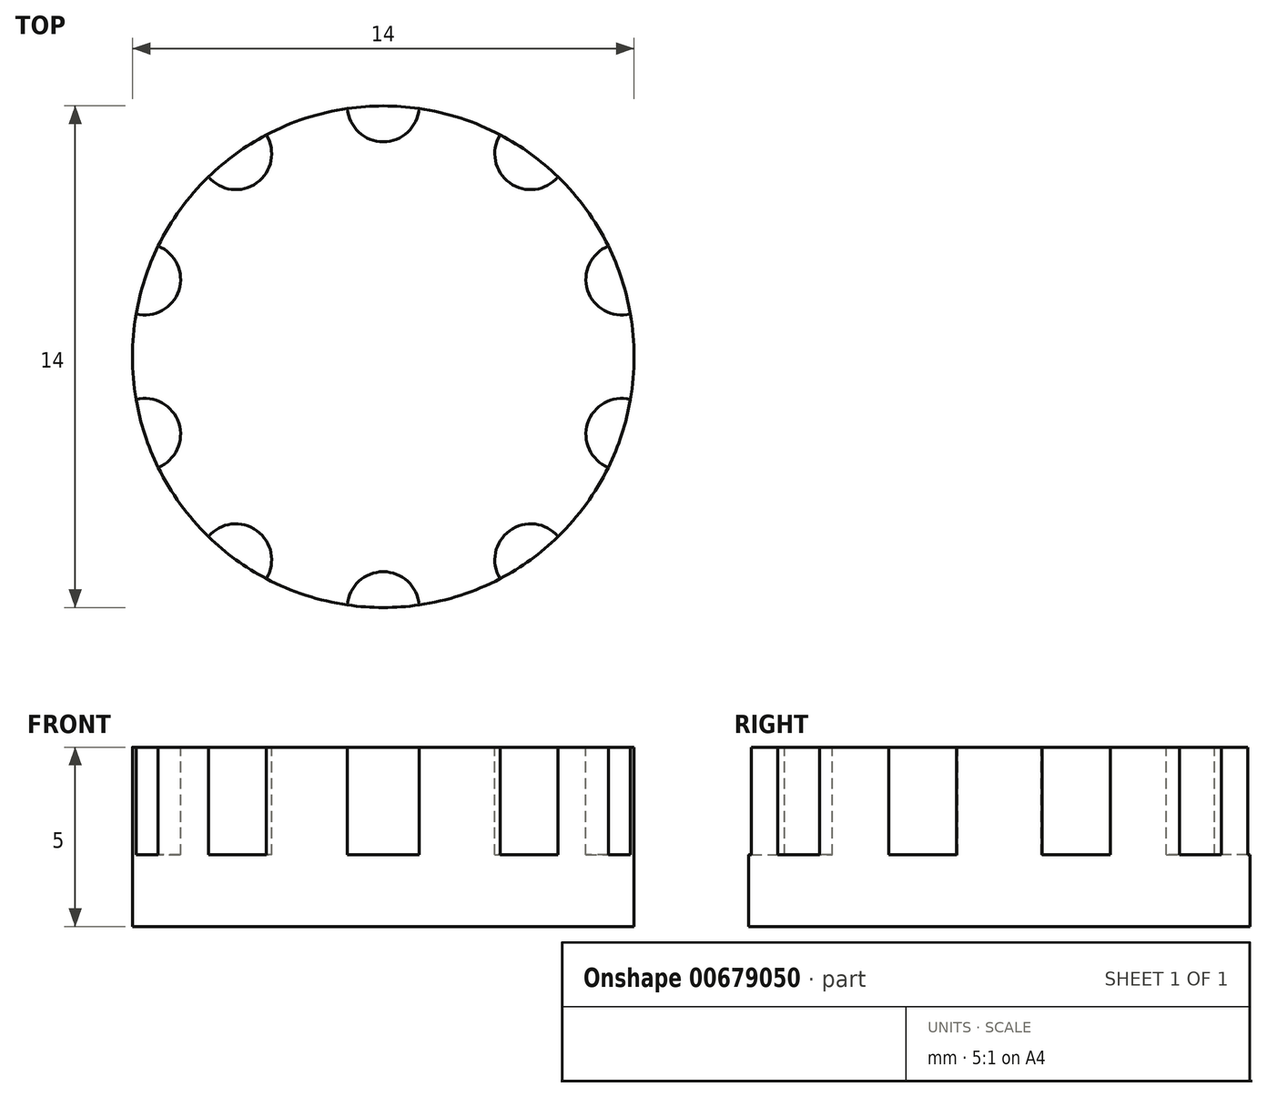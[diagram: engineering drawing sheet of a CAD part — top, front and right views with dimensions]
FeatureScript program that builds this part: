
annotation { "Feature Type Name" : "Feature", "Feature Type Description" : "" }
export const myFeature = defineFeature(function(context is Context, id is Id, definition is map)
    precondition{}
    {
        {
            var Q0;
            Q0=qCreatedBy(makeId("Top.planeOp"),FACE);
            var sketch = newSketch(context, id + "F0", { "sketchPlane" : qUnion([Q0])});
            skCircle(sketch, "E0", {"center": v(0, 0) * mm, "radius": 7 * mm});
            skSolve(sketch);
        }
        {
            var Q0;
            Q0=qSketchRegion(id+"F0",true);
            extrude(context, id + "F1", {"entities" : qUnion([Q0]), "depth" : 5 * mm, "offsetDistance" : 25 * mm});
        }
        {
            var Q0;
            Q0=makeQuery(id+"F1.opExtrude","CAP_FACE",FACE,{"disambiguationData":[OSD([sQuery(id+"F0.wireOp",EDGE,"E0")])],"isStart":false});
            var sketch = newSketch(context, id + "F2", { "sketchPlane" : qUnion([Q0])});
            skArc(sketch, "E1", {"start": v(-1, 6.93) * mm, "mid": v(0, 6) * mm, "end": v(1, 6.93) * mm});
            skArc(sketch, "E2", {"start": v(1, 6.93) * mm, "mid": v(0, 7) * mm, "end": v(-1, 6.93) * mm});
            skArc(sketch, "E3.1.0", {"start": v(-4.88, 5.02) * mm, "mid": v(-3.53, 4.85) * mm, "end": v(-3.27, 6.2) * mm});
            skArc(sketch, "E3.1.1", {"start": v(-3.27, 6.2) * mm, "mid": v(-4.11, 5.66) * mm, "end": v(-4.88, 5.02) * mm});
            skArc(sketch, "E3.2.0", {"start": v(-6.9, 1.2) * mm, "mid": v(-5.7, 1.85) * mm, "end": v(-6.28, 3.09) * mm});
            skArc(sketch, "E3.2.1", {"start": v(-6.28, 3.09) * mm, "mid": v(-6.66, 2.16) * mm, "end": v(-6.9, 1.2) * mm});
            skArc(sketch, "E3.3.0", {"start": v(-6.28, -3.09) * mm, "mid": v(-5.7, -1.85) * mm, "end": v(-6.9, -1.2) * mm});
            skArc(sketch, "E3.3.1", {"start": v(-6.9, -1.2) * mm, "mid": v(-6.66, -2.16) * mm, "end": v(-6.28, -3.09) * mm});
            skArc(sketch, "E3.4.0", {"start": v(-3.27, -6.2) * mm, "mid": v(-3.53, -4.85) * mm, "end": v(-4.88, -5.02) * mm});
            skArc(sketch, "E3.4.1", {"start": v(-4.88, -5.02) * mm, "mid": v(-4.11, -5.66) * mm, "end": v(-3.27, -6.2) * mm});
            skArc(sketch, "E3.5.0", {"start": v(1, -6.93) * mm, "mid": v(0, -6) * mm, "end": v(-1, -6.93) * mm});
            skArc(sketch, "E3.5.1", {"start": v(-1, -6.93) * mm, "mid": v(0, -7) * mm, "end": v(1, -6.93) * mm});
            skArc(sketch, "E3.6.0", {"start": v(4.88, -5.02) * mm, "mid": v(3.53, -4.85) * mm, "end": v(3.27, -6.2) * mm});
            skArc(sketch, "E3.6.1", {"start": v(3.27, -6.2) * mm, "mid": v(4.11, -5.66) * mm, "end": v(4.88, -5.02) * mm});
            skArc(sketch, "E3.7.0", {"start": v(6.9, -1.2) * mm, "mid": v(5.7, -1.85) * mm, "end": v(6.28, -3.09) * mm});
            skArc(sketch, "E3.7.1", {"start": v(6.28, -3.09) * mm, "mid": v(6.66, -2.16) * mm, "end": v(6.9, -1.2) * mm});
            skArc(sketch, "E3.8.0", {"start": v(6.28, 3.09) * mm, "mid": v(5.7, 1.85) * mm, "end": v(6.9, 1.2) * mm});
            skArc(sketch, "E3.8.1", {"start": v(6.9, 1.2) * mm, "mid": v(6.66, 2.16) * mm, "end": v(6.28, 3.09) * mm});
            skArc(sketch, "E3.9.0", {"start": v(3.27, 6.2) * mm, "mid": v(3.53, 4.85) * mm, "end": v(4.88, 5.02) * mm});
            skArc(sketch, "E3.9.1", {"start": v(4.88, 5.02) * mm, "mid": v(4.11, 5.66) * mm, "end": v(3.27, 6.2) * mm});
            skSolve(sketch);
        }
        {
            var Q0;
            Q0=makeQuery(id+"F2.imprint","IMPRINT",FACE,{"disambiguationData":[TD([[makeQuery(id+"F2.imprint","IMPRINT",EDGE,{"derivedFrom":sQuery(id+"F2.wireOp",EDGE,"E1")}),1.0]])]});
            var Q1;
            Q1=makeQuery(id+"F2.imprint","IMPRINT",FACE,{"disambiguationData":[TD([[makeQuery(id+"F2.imprint","IMPRINT",EDGE,{"derivedFrom":sQuery(id+"F2.wireOp",EDGE,"E3.9.0")}),1.0]])]});
            var Q2;
            Q2=makeQuery(id+"F2.imprint","IMPRINT",FACE,{"disambiguationData":[TD([[makeQuery(id+"F2.imprint","IMPRINT",EDGE,{"derivedFrom":sQuery(id+"F2.wireOp",EDGE,"E3.8.0")}),1.0]])]});
            var Q3;
            Q3=makeQuery(id+"F2.imprint","IMPRINT",FACE,{"disambiguationData":[TD([[makeQuery(id+"F2.imprint","IMPRINT",EDGE,{"derivedFrom":sQuery(id+"F2.wireOp",EDGE,"E3.7.0")}),1.0]])]});
            var Q4;
            Q4=makeQuery(id+"F2.imprint","IMPRINT",FACE,{"disambiguationData":[TD([[makeQuery(id+"F2.imprint","IMPRINT",EDGE,{"derivedFrom":sQuery(id+"F2.wireOp",EDGE,"E3.6.0")}),1.0]])]});
            var Q5;
            Q5=makeQuery(id+"F2.imprint","IMPRINT",FACE,{"disambiguationData":[TD([[makeQuery(id+"F2.imprint","IMPRINT",EDGE,{"derivedFrom":sQuery(id+"F2.wireOp",EDGE,"E3.5.0")}),1.0]])]});
            var Q6;
            Q6=makeQuery(id+"F2.imprint","IMPRINT",FACE,{"disambiguationData":[TD([[makeQuery(id+"F2.imprint","IMPRINT",EDGE,{"derivedFrom":sQuery(id+"F2.wireOp",EDGE,"E3.4.0")}),1.0]])]});
            var Q7;
            Q7=makeQuery(id+"F2.imprint","IMPRINT",FACE,{"disambiguationData":[TD([[makeQuery(id+"F2.imprint","IMPRINT",EDGE,{"derivedFrom":sQuery(id+"F2.wireOp",EDGE,"E3.3.0")}),1.0]])]});
            var Q8;
            Q8=makeQuery(id+"F2.imprint","IMPRINT",FACE,{"disambiguationData":[TD([[makeQuery(id+"F2.imprint","IMPRINT",EDGE,{"derivedFrom":sQuery(id+"F2.wireOp",EDGE,"E3.2.0")}),1.0]])]});
            var Q9;
            Q9=makeQuery(id+"F2.imprint","IMPRINT",FACE,{"disambiguationData":[TD([[makeQuery(id+"F2.imprint","IMPRINT",EDGE,{"derivedFrom":sQuery(id+"F2.wireOp",EDGE,"E3.1.0")}),1.0]])]});
            extrude(context, id + "F3", {"entities" : qUnion([Q0, Q1, Q2, Q3, Q4, Q5, Q6, Q7, Q8, Q9]), "operationType" : NewBodyOperationType.REMOVE, "oppositeDirection" : true, "depth" : 3 * mm, "offsetDistance" : 25 * mm});
        }
    });
